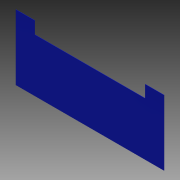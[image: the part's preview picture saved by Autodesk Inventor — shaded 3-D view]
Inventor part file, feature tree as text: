
AUTODESK INVENTOR PART (.ipt)
format: ipt  version: 2013 (Build 170138000, 138)  size: 76,288 bytes
history: native  units: in
note: dims shown in document units (in); Inventor stores cm internally (conversion verified against a paired STEP export)
features: extrude x1, sketch x1
ambient origin geometry x8: Origin, YZ Plane, XZ Plane, XY Plane, X Axis, Y Axis, Z Axis, Center Point
bodies: Solid1 (feature_tree)
feature tree (2):
  extrude  "Extrusion1"  Depth=32.0in
  sketch  "Sketch1"  dims[d0=72.5in d1=32.0in d2=9.25in d3=6.0in d4=9.25in d5=6.0in d6=0.125in d7=0.0in]
